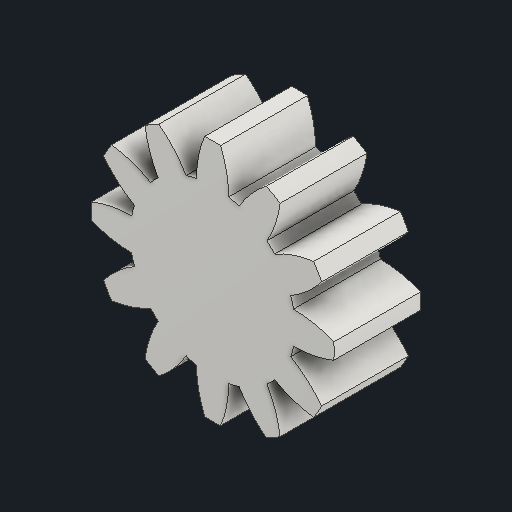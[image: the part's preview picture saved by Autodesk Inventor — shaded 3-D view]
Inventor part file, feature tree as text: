
AUTODESK INVENTOR PART (.ipt)
format: ipt  version: 2024.1 (Build 281209000, 209)  size: 205,312 bytes
history: native  units: mm (DEFAULTED — no unit token found)
features: plane x3, other x3, extrude x1, sketch x1
ambient origin geometry x8: Origin, YZ Plane, XZ Plane, XY Plane, X Axis, Y Axis, Z Axis, Center Point
bodies: Solid1 (feature_tree)
feature tree (8):
  extrude  "Extrusion1"  Depth=3.81mm TaperAngle=0.0deg
  plane  "Work Plane1"
  plane  "Work Plane2"
  plane  "Work Plane3"
  other  "Spur Gear"
  sketch  "Sketch1"  dims[d0=10.668mm d1=3.81mm d2=0.0mm d3=9.144mm d4=76.2mm d5=0.0mm d6=0.0mm d7=15.0deg d9=0.0mm d14=0.0mm d15=23.622mm d16=0.0mm d17=0.0mm d18=0.0mm d19=23.622mm]
  other  "Srf1"
  other  "Pitch Diameter"
